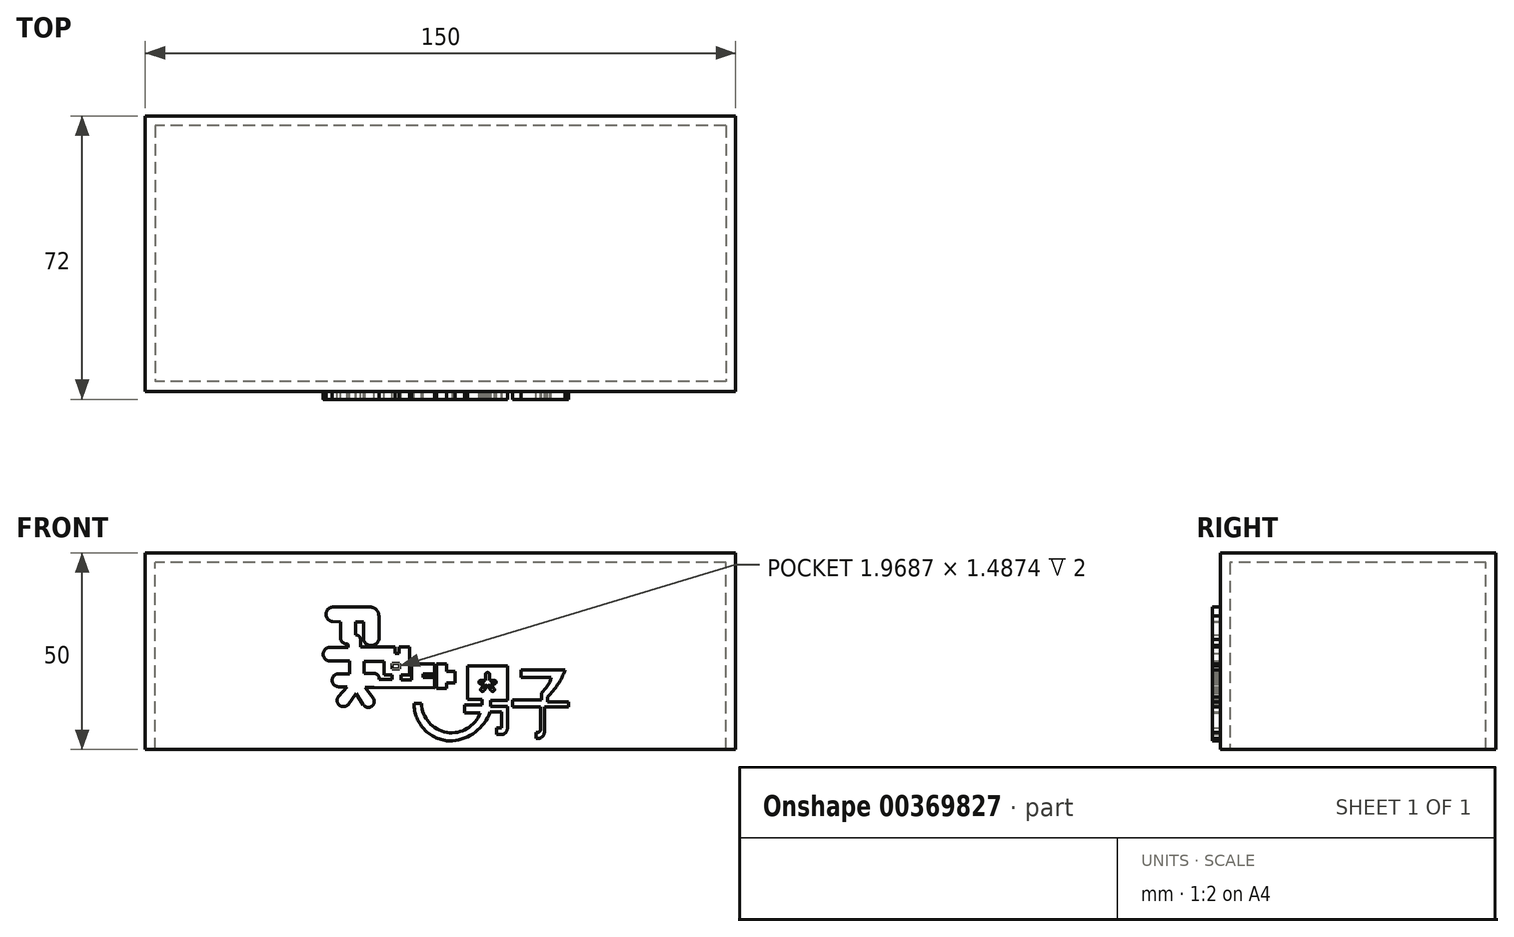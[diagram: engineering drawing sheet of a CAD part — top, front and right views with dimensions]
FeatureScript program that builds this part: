
annotation { "Feature Type Name" : "Feature", "Feature Type Description" : "" }
export const myFeature = defineFeature(function(context is Context, id is Id, definition is map)
    precondition{}
    {
        {
            var Q0;
            Q0=qCreatedBy(makeId("Right.planeOp"),FACE);
            var sketch = newSketch(context, id + "F0", { "sketchPlane" : qUnion([Q0])});
            skLineSegment(sketch, "E0", {"start": v(70, 0) * mm, "end": v(0, 0) * mm});
            skLineSegment(sketch, "E1", {"start": v(70, 0) * mm, "end": v(70, 50) * mm});
            skLineSegment(sketch, "E2", {"start": v(70, 50) * mm, "end": v(0, 50) * mm});
            skLineSegment(sketch, "E3", {"start": v(0, 50) * mm, "end": v(0, 0) * mm});
            skSolve(sketch);
        }
        {
            var Q0;
            Q0=makeQuery(id+"F0.imprint","IMPRINT",FACE,{"disambiguationData":[TD([[makeQuery(id+"F0.imprint","IMPRINT",EDGE,{"derivedFrom":sQuery(id+"F0.wireOp",EDGE,"E0")}),-1.0]])]});
            extrude(context, id + "F1", {"entities" : qUnion([Q0]), "depth" : 150 * mm});
        }
        {
            var Q0;
            Q0=makeQuery(id+"F1.opExtrude","SWEPT_FACE",FACE,{"disambiguationData":[OSD([sQuery(id+"F0.wireOp",EDGE,"E0")])]});
            shell(context, id + "F2", {"entities" : qUnion([Q0]), "thickness" : 2.5 * mm});
        }
        {
            var Q0;
            Q0=qCreatedBy(makeId("Front.planeOp"),FACE);
            var sketch = newSketch(context, id + "F3", { "sketchPlane" : qUnion([Q0])});
            skArc(sketch, "E4", {"start": v(47.46, 36.2) * mm, "mid": v(45.9, 34.3) * mm, "end": v(47.6, 32.53) * mm});
            skLineSegment(sketch, "E5", {"start": v(47.46, 36.2) * mm, "end": v(57.11, 36.2) * mm});
            skArc(sketch, "E6", {"start": v(59.34, 33.92) * mm, "mid": v(58.71, 35.53) * mm, "end": v(57.11, 36.2) * mm});
            skLineSegment(sketch, "E7", {"start": v(59.34, 33.92) * mm, "end": v(59.34, 27.94) * mm});
            skArc(sketch, "E8", {"start": v(55.41, 27.94) * mm, "mid": v(57.37, 26.43) * mm, "end": v(59.34, 27.94) * mm});
            skLineSegment(sketch, "E9", {"start": v(55.41, 27.94) * mm, "end": v(55.41, 32.39) * mm});
            skLineSegment(sketch, "E10", {"start": v(55.41, 32.39) * mm, "end": v(53.43, 32.39) * mm});
            skLineSegment(sketch, "E11", {"start": v(53.43, 32.39) * mm, "end": v(53.43, 27.94) * mm});
            skArc(sketch, "E12", {"start": v(49.58, 27.94) * mm, "mid": v(51.5, 26.78) * mm, "end": v(53.43, 27.94) * mm});
            skLineSegment(sketch, "E13", {"start": v(49.58, 27.94) * mm, "end": v(49.58, 32.39) * mm});
            skLineSegment(sketch, "E14", {"start": v(49.58, 32.39) * mm, "end": v(47.6, 32.53) * mm});
            skLineSegment(sketch, "E15", {"start": v(63.4, 26.1) * mm, "end": v(63.4, 24.47) * mm});
            skLineSegment(sketch, "E16", {"start": v(63.4, 24.47) * mm, "end": v(64.51, 24.47) * mm});
            skLineSegment(sketch, "E17", {"start": v(64.51, 24.47) * mm, "end": v(64.51, 26.1) * mm});
            skLineSegment(sketch, "E18", {"start": v(64.51, 26.1) * mm, "end": v(67.15, 26.1) * mm});
            skLineSegment(sketch, "E19", {"start": v(67.15, 26.1) * mm, "end": v(67.15, 18.92) * mm});
            skLineSegment(sketch, "E20", {"start": v(67.15, 18.92) * mm, "end": v(64.93, 18.92) * mm});
            skLineSegment(sketch, "E21", {"start": v(64.93, 18.92) * mm, "end": v(64.93, 17.67) * mm});
            skLineSegment(sketch, "E22", {"start": v(64.93, 17.67) * mm, "end": v(67.64, 17.67) * mm});
            skLineSegment(sketch, "E23", {"start": v(67.64, 17.67) * mm, "end": v(67.64, 21.8) * mm});
            skLineSegment(sketch, "E24", {"start": v(67.64, 21.8) * mm, "end": v(73.54, 21.8) * mm});
            skLineSegment(sketch, "E25", {"start": v(73.54, 21.8) * mm, "end": v(73.54, 19.23) * mm});
            skLineSegment(sketch, "E26", {"start": v(73.54, 19.23) * mm, "end": v(70.59, 19.23) * mm});
            skLineSegment(sketch, "E27", {"start": v(70.59, 19.23) * mm, "end": v(70.59, 18.36) * mm});
            skLineSegment(sketch, "E28", {"start": v(70.59, 18.36) * mm, "end": v(73.54, 18.36) * mm});
            skLineSegment(sketch, "E29", {"start": v(51.5, 26.78) * mm, "end": v(51.5, 25.97) * mm});
            skLineSegment(sketch, "E30", {"start": v(51.5, 25.97) * mm, "end": v(46.95, 25.97) * mm});
            skArc(sketch, "E31", {"start": v(46.95, 25.97) * mm, "mid": v(45.2, 24.22) * mm, "end": v(46.95, 22.47) * mm});
            skLineSegment(sketch, "E32", {"start": v(46.95, 22.47) * mm, "end": v(51.85, 22.47) * mm});
            skLineSegment(sketch, "E33", {"start": v(51.85, 22.47) * mm, "end": v(51.85, 19.28) * mm});
            skLineSegment(sketch, "E34", {"start": v(51.85, 19.28) * mm, "end": v(49.13, 19.28) * mm});
            skArc(sketch, "E35", {"start": v(49.13, 19.28) * mm, "mid": v(47.47, 17.62) * mm, "end": v(49.13, 15.95) * mm});
            skLineSegment(sketch, "E36", {"start": v(49.13, 15.95) * mm, "end": v(51.23, 15.95) * mm});
            skLineSegment(sketch, "E37", {"start": v(51.23, 15.95) * mm, "end": v(49.13, 13.55) * mm});
            skArc(sketch, "E38", {"start": v(49.13, 13.55) * mm, "mid": v(49.26, 11.32) * mm, "end": v(51.5, 11.4) * mm});
            skLineSegment(sketch, "E39", {"start": v(51.5, 11.4) * mm, "end": v(53.55, 14.25) * mm});
            skLineSegment(sketch, "E40", {"start": v(53.55, 14.25) * mm, "end": v(55.39, 11.4) * mm});
            skArc(sketch, "E41", {"start": v(55.39, 11.4) * mm, "mid": v(57.53, 11) * mm, "end": v(57.84, 13.15) * mm});
            skLineSegment(sketch, "E42", {"start": v(57.84, 13.15) * mm, "end": v(55.8, 15.74) * mm});
            skLineSegment(sketch, "E43", {"start": v(55.8, 15.74) * mm, "end": v(58.15, 15.74) * mm});
            skLineSegment(sketch, "E44", {"start": v(73.54, 18.36) * mm, "end": v(73.54, 15.65) * mm});
            skLineSegment(sketch, "E45", {"start": v(73.54, 15.65) * mm, "end": v(58.15, 15.74) * mm});
            skLineSegment(sketch, "E46", {"start": v(55.56, 22.43) * mm, "end": v(55.56, 19.37) * mm});
            skLineSegment(sketch, "E47", {"start": v(55.56, 19.37) * mm, "end": v(58.15, 19.35) * mm});
            skLineSegment(sketch, "E48", {"start": v(55.56, 22.43) * mm, "end": v(60.68, 22.43) * mm});
            skLineSegment(sketch, "E49", {"start": v(60.68, 22.43) * mm, "end": v(60.68, 19.02) * mm});
            skLineSegment(sketch, "E50", {"start": v(60.68, 19.02) * mm, "end": v(62.7, 19.02) * mm});
            skLineSegment(sketch, "E51", {"start": v(62.7, 19.02) * mm, "end": v(62.7, 17.88) * mm});
            skLineSegment(sketch, "E52", {"start": v(62.7, 17.88) * mm, "end": v(59.41, 17.88) * mm});
            skArc(sketch, "E53", {"start": v(59.41, 17.88) * mm, "mid": v(59.11, 18.9) * mm, "end": v(58.15, 19.35) * mm});
            skLineSegment(sketch, "E54", {"start": v(62.7, 21.9) * mm, "end": v(62.7, 20.46) * mm});
            skLineSegment(sketch, "E55", {"start": v(62.7, 20.46) * mm, "end": v(64.66, 20.46) * mm});
            skLineSegment(sketch, "E56", {"start": v(64.66, 20.46) * mm, "end": v(64.66, 21.95) * mm});
            skLineSegment(sketch, "E57", {"start": v(64.66, 21.95) * mm, "end": v(62.7, 21.9) * mm});
            skLineSegment(sketch, "E58", {"start": v(74.03, 21.8) * mm, "end": v(74.03, 15.53) * mm});
            skLineSegment(sketch, "E59", {"start": v(74.03, 15.53) * mm, "end": v(76.5, 15.53) * mm});
            skLineSegment(sketch, "E60", {"start": v(76.5, 15.53) * mm, "end": v(76.5, 16.97) * mm});
            skLineSegment(sketch, "E61", {"start": v(76.5, 16.97) * mm, "end": v(78.67, 16.97) * mm});
            skLineSegment(sketch, "E62", {"start": v(78.67, 16.97) * mm, "end": v(78.67, 19.83) * mm});
            skLineSegment(sketch, "E63", {"start": v(78.67, 19.83) * mm, "end": v(76.5, 19.83) * mm});
            skLineSegment(sketch, "E64", {"start": v(76.5, 19.83) * mm, "end": v(76.5, 21.8) * mm});
            skLineSegment(sketch, "E65", {"start": v(74.03, 21.8) * mm, "end": v(76.5, 21.8) * mm});
            skLineSegment(sketch, "E66", {"start": v(92, 21.27) * mm, "end": v(81.88, 21.27) * mm});
            skLineSegment(sketch, "E67", {"start": v(81.88, 21.27) * mm, "end": v(81.88, 12.75) * mm});
            skLineSegment(sketch, "E68", {"start": v(81.88, 12.75) * mm, "end": v(85.5, 12.75) * mm});
            skLineSegment(sketch, "E69", {"start": v(85.5, 12.75) * mm, "end": v(85.5, 11.35) * mm});
            skLineSegment(sketch, "E70", {"start": v(85.5, 11.35) * mm, "end": v(81.18, 11.35) * mm});
            skLineSegment(sketch, "E71", {"start": v(81.18, 11.35) * mm, "end": v(81.18, 9.63) * mm});
            skLineSegment(sketch, "E72", {"start": v(92, 21.27) * mm, "end": v(92, 12.5) * mm});
            skLineSegment(sketch, "E73", {"start": v(92, 12.5) * mm, "end": v(87.77, 12.5) * mm});
            skLineSegment(sketch, "E74", {"start": v(87.77, 12.5) * mm, "end": v(87.77, 11) * mm});
            skLineSegment(sketch, "E75", {"start": v(87.77, 11) * mm, "end": v(92, 11) * mm});
            skLineSegment(sketch, "E76", {"start": v(92, 11) * mm, "end": v(92, 5.42) * mm});
            skArc(sketch, "E77", {"start": v(90.69, 3.8) * mm, "mid": v(91.63, 4.38) * mm, "end": v(92, 5.42) * mm});
            skLineSegment(sketch, "E78", {"start": v(90.69, 3.8) * mm, "end": v(89.18, 3.8) * mm});
            skLineSegment(sketch, "E79", {"start": v(89.18, 3.8) * mm, "end": v(89.18, 5.51) * mm});
            skLineSegment(sketch, "E80", {"start": v(89.18, 5.51) * mm, "end": v(90.47, 5.51) * mm});
            skLineSegment(sketch, "E81", {"start": v(90.47, 5.51) * mm, "end": v(90.47, 9.53) * mm});
            skLineSegment(sketch, "E82", {"start": v(90.47, 9.53) * mm, "end": v(87.6, 9.53) * mm});
            skArc(sketch, "E83", {"start": v(68.29, 11.72) * mm, "mid": v(71.12, 4.87) * mm, "end": v(78.02, 2.2) * mm});
            skLineSegment(sketch, "E84", {"start": v(68.29, 11.72) * mm, "end": v(70.15, 11.72) * mm});
            skLineSegment(sketch, "E85", {"start": v(85.08, 9.34) * mm, "end": v(81.18, 9.34) * mm});
            skLineSegment(sketch, "E86", {"start": v(81.18, 9.34) * mm, "end": v(81.18, 9.63) * mm});
            skArc(sketch, "E87", {"start": v(78.02, 2.2) * mm, "mid": v(83.87, 4.47) * mm, "end": v(87.6, 9.53) * mm});
            skLineSegment(sketch, "E88", {"start": v(95.46, 20.2) * mm, "end": v(95.46, 18.35) * mm});
            skLineSegment(sketch, "E89", {"start": v(95.46, 18.35) * mm, "end": v(101.58, 18.35) * mm});
            skLineSegment(sketch, "E90", {"start": v(102.85, 17.14) * mm, "end": v(101.78, 15.61) * mm});
            skLineSegment(sketch, "E91", {"start": v(100.62, 14.34) * mm, "end": v(100.62, 12.6) * mm});
            skLineSegment(sketch, "E92", {"start": v(100.62, 12.6) * mm, "end": v(93.34, 12.6) * mm});
            skLineSegment(sketch, "E93", {"start": v(93.34, 12.6) * mm, "end": v(93.34, 10.86) * mm});
            skLineSegment(sketch, "E94", {"start": v(93.34, 10.86) * mm, "end": v(100.42, 10.86) * mm});
            skLineSegment(sketch, "E95", {"start": v(100.42, 10.86) * mm, "end": v(100.42, 5.2) * mm});
            skArc(sketch, "E96", {"start": v(99.25, 4.37) * mm, "mid": v(100.05, 4.48) * mm, "end": v(100.42, 5.2) * mm});
            skLineSegment(sketch, "E97", {"start": v(99.25, 4.37) * mm, "end": v(99.25, 2.9) * mm});
            skArc(sketch, "E98", {"start": v(99.25, 2.9) * mm, "mid": v(100.69, 3.1) * mm, "end": v(101.4, 4.37) * mm});
            skLineSegment(sketch, "E99", {"start": v(101.4, 4.37) * mm, "end": v(101.4, 10.86) * mm});
            skLineSegment(sketch, "E100", {"start": v(101.4, 10.86) * mm, "end": v(107.56, 10.86) * mm});
            skLineSegment(sketch, "E101", {"start": v(107.56, 10.86) * mm, "end": v(107.56, 12.1) * mm});
            skLineSegment(sketch, "E102", {"start": v(107.56, 12.1) * mm, "end": v(102.21, 12.1) * mm});
            skLineSegment(sketch, "E103", {"start": v(102.21, 12.1) * mm, "end": v(102.21, 13.34) * mm});
            skArc(sketch, "E104", {"start": v(102.21, 13.34) * mm, "mid": v(104.8, 16.53) * mm, "end": v(106.65, 20.2) * mm});
            skLineSegment(sketch, "E105", {"start": v(95.46, 20.2) * mm, "end": v(106.65, 20.2) * mm});
            skLineSegment(sketch, "E106", {"start": v(101.58, 18.35) * mm, "end": v(103.03, 18.35) * mm});
            skLineSegment(sketch, "E107", {"start": v(103.03, 18.35) * mm, "end": v(102.85, 17.14) * mm});
            skLineSegment(sketch, "E108", {"start": v(101.78, 15.61) * mm, "end": v(100.62, 14.34) * mm});
            skLineSegment(sketch, "E109", {"start": v(63.4, 26.1) * mm, "end": v(54.68, 26.1) * mm});
            skLineSegment(sketch, "E110", {"start": v(54.68, 26.1) * mm, "end": v(54.68, 27.94) * mm});
            skArc(sketch, "E111", {"start": v(54.68, 27.94) * mm, "mid": v(54.31, 28.8) * mm, "end": v(53.43, 29.12) * mm});
            skPoint(sketch, "E112.endSnap0", {"position": v(83.98, 16.86) * mm});
            skLineSegment(sketch, "E113", {"start": v(90.08, 19.31) * mm, "end": v(87.5, 19.31) * mm});
            skLineSegment(sketch, "E114", {"start": v(83.98, 19.31) * mm, "end": v(86.43, 19.31) * mm});
            skArc(sketch, "E115", {"start": v(87.5, 18.9) * mm, "mid": v(86.96, 19.57) * mm, "end": v(86.43, 18.9) * mm});
            skLineSegment(sketch, "E116", {"start": v(86.43, 18.9) * mm, "end": v(86.43, 17.54) * mm});
            skLineSegment(sketch, "E117", {"start": v(86.43, 17.54) * mm, "end": v(85.16, 17.54) * mm});
            skArc(sketch, "E118", {"start": v(85.16, 17.54) * mm, "mid": v(84.75, 17.13) * mm, "end": v(85.16, 16.72) * mm});
            skLineSegment(sketch, "E119", {"start": v(85.16, 16.72) * mm, "end": v(86.24, 16.72) * mm});
            skLineSegment(sketch, "E120", {"start": v(86.24, 16.72) * mm, "end": v(85.3, 15.5) * mm});
            skLineSegment(sketch, "E121", {"start": v(83.98, 19.31) * mm, "end": v(83.98, 14.82) * mm});
            skLineSegment(sketch, "E122", {"start": v(83.98, 14.82) * mm, "end": v(85.01, 14.82) * mm});
            skLineSegment(sketch, "E123", {"start": v(86.19, 14.82) * mm, "end": v(87.76, 14.82) * mm});
            skLineSegment(sketch, "E124", {"start": v(88.9, 14.82) * mm, "end": v(90.08, 14.82) * mm});
            skLineSegment(sketch, "E125", {"start": v(90.08, 14.82) * mm, "end": v(90.08, 19.31) * mm});
            skArc(sketch, "E126", {"start": v(85.3, 15.5) * mm, "mid": v(85.47, 14.82) * mm, "end": v(86.1, 15.14) * mm});
            skLineSegment(sketch, "E127", {"start": v(85.01, 14.82) * mm, "end": v(85.48, 14.82) * mm});
            skLineSegment(sketch, "E128", {"start": v(86.19, 14.82) * mm, "end": v(85.83, 14.82) * mm});
            skLineSegment(sketch, "E129", {"start": v(86.96, 19.57) * mm, "end": v(86.96, 14.82) * mm, "construction": true});
            skLineSegment(sketch, "E130", {"start": v(86.1, 15.14) * mm, "end": v(86.96, 16.53) * mm});
            skLineSegment(sketch, "E131.MirrorCS", {"start": v(87.5, 18.9) * mm, "end": v(87.5, 17.54) * mm});
            skLineSegment(sketch, "E132.MirrorCS", {"start": v(87.5, 17.54) * mm, "end": v(88.76, 17.54) * mm});
            skArc(sketch, "E133.MirrorCS", {"start": v(88.76, 17.54) * mm, "mid": v(89.17, 17.13) * mm, "end": v(88.76, 16.72) * mm});
            skLineSegment(sketch, "E134.MirrorCS", {"start": v(88.76, 16.72) * mm, "end": v(87.68, 16.72) * mm});
            skLineSegment(sketch, "E135.MirrorCS", {"start": v(87.68, 16.72) * mm, "end": v(88.62, 15.5) * mm});
            skArc(sketch, "E136.MirrorCS", {"start": v(88.62, 15.5) * mm, "mid": v(88.45, 14.82) * mm, "end": v(87.83, 15.14) * mm});
            skLineSegment(sketch, "E137.MirrorCS", {"start": v(87.83, 15.14) * mm, "end": v(86.96, 16.53) * mm});
            skLineSegment(sketch, "E138", {"start": v(88.9, 14.82) * mm, "end": v(88.44, 14.82) * mm});
            skLineSegment(sketch, "E139", {"start": v(87.76, 14.82) * mm, "end": v(88.09, 14.82) * mm});
            skArc(sketch, "E140", {"start": v(70.15, 11.72) * mm, "mid": v(76.63, 4.36) * mm, "end": v(85.08, 9.34) * mm});
            skSolve(sketch);
        }
        {
            var Q0;
            Q0=makeQuery(id+"F3.imprint","IMPRINT",FACE,{"disambiguationData":[TD([[makeQuery(id+"F3.imprint","IMPRINT",EDGE,{"derivedFrom":sQuery(id+"F3.wireOp",EDGE,"E4")}),1.0]])]});
            var Q1;
            Q1=makeQuery(id+"F3.imprint","IMPRINT",FACE,{"disambiguationData":[TD([[makeQuery(id+"F3.imprint","IMPRINT",EDGE,{"derivedFrom":sQuery(id+"F3.wireOp",EDGE,"E15")}),-1.0]])]});
            var Q2;
            Q2=makeQuery(id+"F3.imprint","IMPRINT",FACE,{"disambiguationData":[TD([[makeQuery(id+"F3.imprint","IMPRINT",EDGE,{"derivedFrom":sQuery(id+"F3.wireOp",EDGE,"E58")}),1.0]])]});
            var Q3;
            Q3=makeQuery(id+"F3.imprint","IMPRINT",FACE,{"disambiguationData":[TD([[makeQuery(id+"F3.imprint","IMPRINT",EDGE,{"derivedFrom":sQuery(id+"F3.wireOp",EDGE,"E66")}),1.0]])]});
            var Q4;
            Q4=makeQuery(id+"F3.imprint","IMPRINT",FACE,{"disambiguationData":[TD([[makeQuery(id+"F3.imprint","IMPRINT",EDGE,{"derivedFrom":sQuery(id+"F3.wireOp",EDGE,"E88")}),1.0]])]});
            var Q5;
            Q5=makeQuery(id+"F3.imprint","IMPRINT",FACE,{"disambiguationData":[TD([[makeQuery(id+"F3.imprint","IMPRINT",EDGE,{"derivedFrom":sQuery(id+"F3.wireOp",EDGE,"E123")}),1.0]])]});
            var Q6;
            Q6=sQuery(id+"F3.wireOp",EDGE,"E99");
            var Q7;
            Q7=sQuery(id+"F3.wireOp",EDGE,"E95");
            var Q8;
            Q8=sQuery(id+"F3.wireOp",EDGE,"E100");
            var Q9;
            Q9=sQuery(id+"F3.wireOp",EDGE,"E102");
            var Q10;
            Q10=sQuery(id+"F3.wireOp",EDGE,"E103");
            var Q11;
            Q11=sQuery(id+"F3.wireOp",EDGE,"E104");
            var Q12;
            Q12=sQuery(id+"F3.wireOp",EDGE,"E105");
            var Q13;
            Q13=sQuery(id+"F3.wireOp",EDGE,"E88");
            var Q14;
            Q14=sQuery(id+"F3.wireOp",EDGE,"E89");
            var Q15;
            Q15=sQuery(id+"F3.wireOp",EDGE,"E107");
            var Q16;
            Q16=sQuery(id+"F3.wireOp",EDGE,"E106");
            var Q17;
            Q17=sQuery(id+"F3.wireOp",EDGE,"E90");
            var Q18;
            Q18=sQuery(id+"F3.wireOp",EDGE,"E108");
            var Q19;
            Q19=sQuery(id+"F3.wireOp",EDGE,"E91");
            var Q20;
            Q20=sQuery(id+"F3.wireOp",EDGE,"E92");
            var Q21;
            Q21=sQuery(id+"F3.wireOp",EDGE,"E94");
            var Q22;
            Q22=sQuery(id+"F3.wireOp",EDGE,"E93");
            var Q23;
            Q23=sQuery(id+"F3.wireOp",EDGE,"E96");
            var Q24;
            Q24=sQuery(id+"F3.wireOp",EDGE,"E97");
            var Q25;
            Q25=sQuery(id+"F3.wireOp",EDGE,"E98");
            var Q26;
            Q26=sQuery(id+"F3.wireOp",EDGE,"E76");
            var Q27;
            Q27=sQuery(id+"F3.wireOp",EDGE,"E81");
            var Q28;
            Q28=sQuery(id+"F3.wireOp",EDGE,"E82");
            var Q29;
            Q29=sQuery(id+"F3.wireOp",EDGE,"E80");
            var Q30;
            Q30=sQuery(id+"F3.wireOp",EDGE,"E79");
            var Q31;
            Q31=sQuery(id+"F3.wireOp",EDGE,"E77");
            var Q32;
            Q32=sQuery(id+"F3.wireOp",EDGE,"E78");
            var Q33;
            Q33=sQuery(id+"F3.wireOp",EDGE,"E75");
            var Q34;
            Q34=sQuery(id+"F3.wireOp",EDGE,"E74");
            var Q35;
            Q35=sQuery(id+"F3.wireOp",EDGE,"E73");
            var Q36;
            Q36=sQuery(id+"F3.wireOp",EDGE,"E72");
            var Q37;
            Q37=sQuery(id+"F3.wireOp",EDGE,"E66");
            var Q38;
            Q38=sQuery(id+"F3.wireOp",EDGE,"DhTE4iAD-ulyw-uvaz-Bk8E-K0Hv8bPboK2H");
            var Q39;
            Q39=sQuery(id+"F3.wireOp",EDGE,"lB3TDaJu-STJq-ZHVc-RRf2-kNd6A1pyXpnO");
            var Q40;
            Q40=sQuery(id+"F3.wireOp",EDGE,"kwcdbift-VeJw-Ueot-iuPh-4M3SW9WsVoVE");
            var Q41;
            Q41=sQuery(id+"F3.wireOp",EDGE,"XVgMBL9d-t8tC-MEo2-fzin-ABwYbVmtihmD");
            var Q42;
            Q42=sQuery(id+"F3.wireOp",EDGE,"0z2Cnq0L-dYOV-wUEp-eOrI-tJ3lY36Or7HN");
            var Q43;
            Q43=sQuery(id+"F3.wireOp",EDGE,"771AcnBi-ktMi-haKf-tugn-cHGy0MpebzqT");
            var Q44;
            Q44=sQuery(id+"F3.wireOp",EDGE,"ac33XvrS-RFz3-YmKe-4wfF-Lk6hu8ZCxfvN");
            var Q45;
            Q45=sQuery(id+"F3.wireOp",EDGE,"9aa2ed82-bae8-4713-a8dc-43e22c909e5d");
            var Q46;
            Q46=sQuery(id+"F3.wireOp",EDGE,"rhyEyB0k-fIWE-kWsF-eTtw-KBZc5tZFxACj");
            var Q47;
            Q47=sQuery(id+"F3.wireOp",EDGE,"DQliAK6u-PvsD-jDZn-0GHR-853VbfoqICiv");
            var Q48;
            Q48=sQuery(id+"F3.wireOp",EDGE,"N1xTG34J-nXhw-1D47-g8LI-0tFNMYgvPNez");
            var Q49;
            Q49=sQuery(id+"F3.wireOp",EDGE,"ec8627f9-251c-4a3a-8574-6a841f900925");
            var Q50;
            Q50=sQuery(id+"F3.wireOp",EDGE,"E67");
            var Q51;
            Q51=sQuery(id+"F3.wireOp",EDGE,"E68");
            var Q52;
            Q52=sQuery(id+"F3.wireOp",EDGE,"E69");
            var Q53;
            Q53=sQuery(id+"F3.wireOp",EDGE,"E70");
            var Q54;
            Q54=sQuery(id+"F3.wireOp",EDGE,"E71");
            var Q55;
            Q55=sQuery(id+"F3.wireOp",EDGE,"E85");
            var Q56;
            Q56=sQuery(id+"F3.wireOp",EDGE,"XC85punv-0KQ3-6zMq-Q4Gf-n2bXdbHIlexh");
            var Q57;
            Q57=sQuery(id+"F3.wireOp",EDGE,"E87");
            var Q58;
            Q58=sQuery(id+"F3.wireOp",EDGE,"E83");
            var Q59;
            Q59=sQuery(id+"F3.wireOp",EDGE,"E84");
            var Q60;
            Q60=sQuery(id+"F3.wireOp",EDGE,"E62");
            var Q61;
            Q61=sQuery(id+"F3.wireOp",EDGE,"E61");
            var Q62;
            Q62=sQuery(id+"F3.wireOp",EDGE,"E63");
            var Q63;
            Q63=sQuery(id+"F3.wireOp",EDGE,"E65");
            var Q64;
            Q64=sQuery(id+"F3.wireOp",EDGE,"E64");
            var Q65;
            Q65=sQuery(id+"F3.wireOp",EDGE,"E60");
            var Q66;
            Q66=sQuery(id+"F3.wireOp",EDGE,"E59");
            var Q67;
            Q67=sQuery(id+"F3.wireOp",EDGE,"E58");
            var Q68;
            Q68=sQuery(id+"F3.wireOp",EDGE,"E44");
            var Q69;
            Q69=sQuery(id+"F3.wireOp",EDGE,"E25");
            var Q70;
            Q70=sQuery(id+"F3.wireOp",EDGE,"E24");
            var Q71;
            Q71=sQuery(id+"F3.wireOp",EDGE,"E26");
            var Q72;
            Q72=sQuery(id+"F3.wireOp",EDGE,"E27");
            var Q73;
            Q73=sQuery(id+"F3.wireOp",EDGE,"E28");
            var Q74;
            Q74=sQuery(id+"F3.wireOp",EDGE,"E45");
            var Q75;
            Q75=sQuery(id+"F3.wireOp",EDGE,"E23");
            var Q76;
            Q76=sQuery(id+"F3.wireOp",EDGE,"E19");
            var Q77;
            Q77=sQuery(id+"F3.wireOp",EDGE,"E20");
            var Q78;
            Q78=sQuery(id+"F3.wireOp",EDGE,"E22");
            var Q79;
            Q79=sQuery(id+"F3.wireOp",EDGE,"E21");
            var Q80;
            Q80=sQuery(id+"F3.wireOp",EDGE,"E18");
            var Q81;
            Q81=sQuery(id+"F3.wireOp",EDGE,"E17");
            var Q82;
            Q82=sQuery(id+"F3.wireOp",EDGE,"E16");
            var Q83;
            Q83=sQuery(id+"F3.wireOp",EDGE,"E15");
            var Q84;
            Q84=sQuery(id+"F3.wireOp",EDGE,"E57");
            var Q85;
            Q85=sQuery(id+"F3.wireOp",EDGE,"E56");
            var Q86;
            Q86=sQuery(id+"F3.wireOp",EDGE,"E55");
            var Q87;
            Q87=sQuery(id+"F3.wireOp",EDGE,"E54");
            var Q88;
            Q88=sQuery(id+"F3.wireOp",EDGE,"E51");
            var Q89;
            Q89=sQuery(id+"F3.wireOp",EDGE,"E50");
            var Q90;
            Q90=sQuery(id+"F3.wireOp",EDGE,"E52");
            var Q91;
            Q91=sQuery(id+"F3.wireOp",EDGE,"E53");
            var Q92;
            Q92=sQuery(id+"F3.wireOp",EDGE,"E47");
            var Q93;
            Q93=sQuery(id+"F3.wireOp",EDGE,"E33");
            var Q94;
            Q94=sQuery(id+"F3.wireOp",EDGE,"E46");
            var Q95;
            Q95=sQuery(id+"F3.wireOp",EDGE,"E43");
            var Q96;
            Q96=sQuery(id+"F3.wireOp",EDGE,"E42");
            var Q97;
            Q97=sQuery(id+"F3.wireOp",EDGE,"E41");
            var Q98;
            Q98=sQuery(id+"F3.wireOp",EDGE,"E40");
            var Q99;
            Q99=sQuery(id+"F3.wireOp",EDGE,"E39");
            var Q100;
            Q100=sQuery(id+"F3.wireOp",EDGE,"E38");
            var Q101;
            Q101=sQuery(id+"F3.wireOp",EDGE,"E37");
            var Q102;
            Q102=sQuery(id+"F3.wireOp",EDGE,"E36");
            var Q103;
            Q103=sQuery(id+"F3.wireOp",EDGE,"E35");
            var Q104;
            Q104=sQuery(id+"F3.wireOp",EDGE,"E34");
            var Q105;
            Q105=sQuery(id+"F3.wireOp",EDGE,"E48");
            var Q106;
            Q106=sQuery(id+"F3.wireOp",EDGE,"bTNjpxmW-5fSY-2Uxo-KrR1-2mbPFDydBwHu");
            var Q107;
            Q107=sQuery(id+"F3.wireOp",EDGE,"YquDIioR-X5Px-GkiG-F79y-yXCEPXPeYJbw");
            var Q108;
            Q108=sQuery(id+"F3.wireOp",EDGE,"RtvcVmeW-3UPS-rm0l-SQWU-nZyYZJheNu9b");
            var Q109;
            Q109=sQuery(id+"F3.wireOp",EDGE,"E12");
            var Q110;
            Q110=sQuery(id+"F3.wireOp",EDGE,"E29");
            var Q111;
            Q111=sQuery(id+"F3.wireOp",EDGE,"E11");
            var Q112;
            Q112=sQuery(id+"F3.wireOp",EDGE,"E30");
            var Q113;
            Q113=sQuery(id+"F3.wireOp",EDGE,"E31");
            var Q114;
            Q114=sQuery(id+"F3.wireOp",EDGE,"E32");
            var Q115;
            Q115=sQuery(id+"F3.wireOp",EDGE,"E13");
            var Q116;
            Q116=sQuery(id+"F3.wireOp",EDGE,"E9");
            var Q117;
            Q117=sQuery(id+"F3.wireOp",EDGE,"E8");
            var Q118;
            Q118=sQuery(id+"F3.wireOp",EDGE,"E7");
            var Q119;
            Q119=sQuery(id+"F3.wireOp",EDGE,"E10");
            var Q120;
            Q120=sQuery(id+"F3.wireOp",EDGE,"E6");
            var Q121;
            Q121=sQuery(id+"F3.wireOp",EDGE,"E5");
            var Q122;
            Q122=sQuery(id+"F3.wireOp",EDGE,"E4");
            var Q123;
            Q123=sQuery(id+"F3.wireOp",EDGE,"E14");
            extrude(context, id + "F4", {"entities" : qUnion([Q0, Q1, Q2, Q3, Q4, Q5]), "operationType" : NewBodyOperationType.ADD, "flatOperationType" : FlatOperationType.REMOVE, "surfaceEntities" : qUnion([Q6, Q7, Q8, Q9, Q10, Q11, Q12, Q13, Q14, Q15, Q16, Q17, Q18, Q19, Q20, Q21, Q22, Q23, Q24, Q25, Q26, Q27, Q28, Q29, Q30, Q31, Q32, Q33, Q34, Q35, Q36, Q37, Q38, Q39, Q40, Q41, Q42, Q43, Q44, Q45, Q46, Q47, Q48, Q49, Q50, Q51, Q52, Q53, Q54, Q55, Q56, Q57, Q58, Q59, Q60, Q61, Q62, Q63, Q64, Q65, Q66, Q67, Q68, Q69, Q70, Q71, Q72, Q73, Q74, Q75, Q76, Q77, Q78, Q79, Q80, Q81, Q82, Q83, Q84, Q85, Q86, Q87, Q88, Q89, Q90, Q91, Q92, Q93, Q94, Q95, Q96, Q97, Q98, Q99, Q100, Q101, Q102, Q103, Q104, Q105, Q106, Q107, Q108, Q109, Q110, Q111, Q112, Q113, Q114, Q115, Q116, Q117, Q118, Q119, Q120, Q121, Q122, Q123]), "offsetDistance" : 25 * mm, "depth" : 2 * mm, "domain" : OperationDomain.MODEL});
        }
    });
